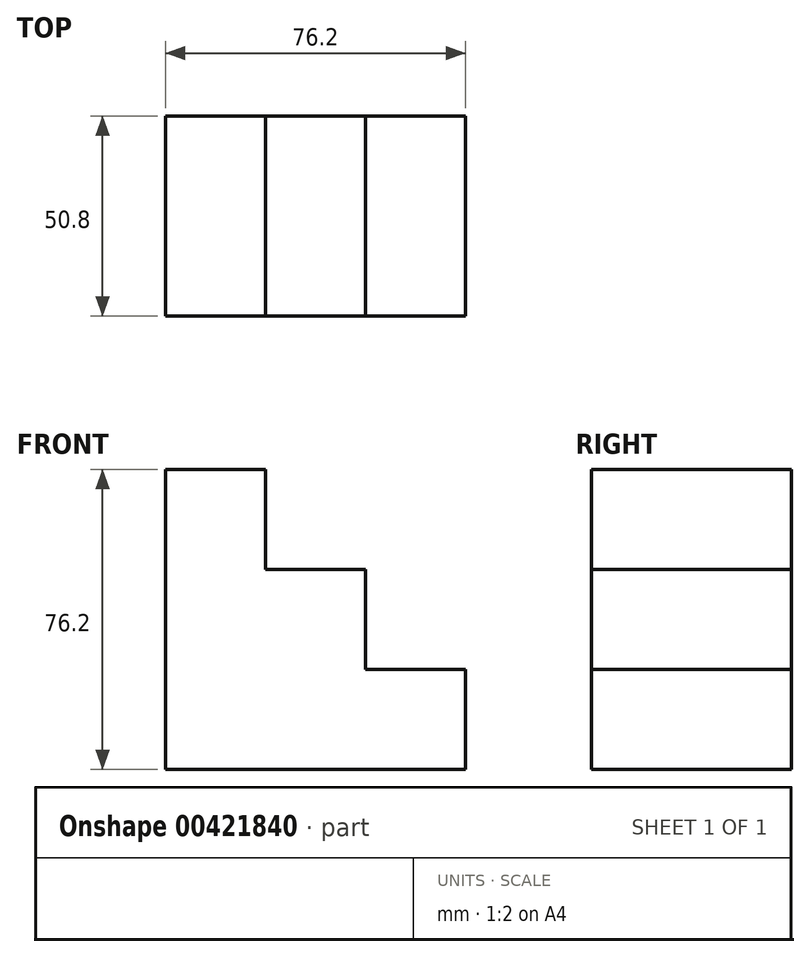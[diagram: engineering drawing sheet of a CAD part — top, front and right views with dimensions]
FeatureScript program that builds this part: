
annotation { "Feature Type Name" : "Feature", "Feature Type Description" : "" }
export const myFeature = defineFeature(function(context is Context, id is Id, definition is map)
    precondition{}
    {
        {
            var Q0;
            Q0=qCreatedBy(makeId("Front.planeOp"),FACE);
            var sketch = newSketch(context, id + "F0", { "sketchPlane" : qUnion([Q0])});
            skLineSegment(sketch, "E0", {"start": v(0, 0) * mm, "end": v(0, 76.2) * mm});
            skLineSegment(sketch, "E1", {"start": v(0, 0) * mm, "end": v(76.2, 0) * mm});
            skLineSegment(sketch, "E2", {"start": v(0, 76.2) * mm, "end": v(25.4, 76.2) * mm});
            skLineSegment(sketch, "E3", {"start": v(25.4, 76.2) * mm, "end": v(25.4, 50.8) * mm});
            skLineSegment(sketch, "E4", {"start": v(25.4, 50.8) * mm, "end": v(50.8, 50.8) * mm});
            skLineSegment(sketch, "E5", {"start": v(50.8, 50.8) * mm, "end": v(50.8, 25.4) * mm});
            skLineSegment(sketch, "E6", {"start": v(50.8, 25.4) * mm, "end": v(76.2, 25.4) * mm});
            skLineSegment(sketch, "E7", {"start": v(76.2, 25.4) * mm, "end": v(76.2, 0) * mm});
            skSolve(sketch);
        }
        {
            var Q0;
            Q0=makeQuery(id+"F0.imprint","IMPRINT",FACE,{"disambiguationData":[TD([[makeQuery(id+"F0.imprint","IMPRINT",EDGE,{"derivedFrom":sQuery(id+"F0.wireOp",EDGE,"E0")}),-1.0]])]});
            extrude(context, id + "F1", {"entities" : qUnion([Q0]), "depth" : 50.8 * mm});
        }
    });
